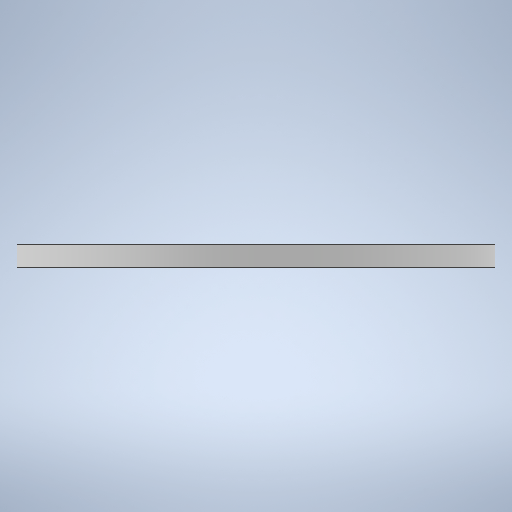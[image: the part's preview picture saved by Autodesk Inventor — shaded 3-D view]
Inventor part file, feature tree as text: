
AUTODESK INVENTOR PART (.ipt)
format: ipt  version: 2025.2 (Build 292293000, 293)  size: 529,408 bytes
history: native  units: in
note: dims shown in document units (in); Inventor stores cm internally (conversion verified against a paired STEP export)
features: sketch x7, extrude x5, hole x1, revolve x1
ambient origin geometry x8: Origin, YZ Plane, XZ Plane, XY Plane, X Axis, Y Axis, Z Axis, Center Point
bodies: Solid1 (feature_tree)
feature tree (14):
  sketch  "Sketch1"  dims[d0=11.811in d1=7.874in]
  extrude  "Extrusion1"  Depth=7.874in
  extrude  "Extrusion3"  Depth=0.0787in
  extrude  "Extrusion4"  Depth=3.937in TaperAngle=360.0deg
  sketch  "Sketch3"  dims[d14=0.2343in d15=3.937in d17=360.0deg]
  extrude  "Extrusion5"  Depth=11.0236in
  hole  "Hole1"  [1 undecoded]
  revolve  "Revolution1"  [1 undecoded]
  extrude  "Extrusion6"  Depth=0.0837in TaperAngle=0.0deg
  sketch  "Sketch Circular Pattern2"  dims[d8=0.0787in d9=0.0in d13=9.8425in]
  sketch  "Sketch Circular Pattern3"  dims[d19=9.498in d20=11.0236in]
  sketch  "Sketch4"  dims[d21=0.2343in d23=3.937in d25=360.0deg]
  sketch  "Sketch5"  dims[d27=0.1673in d28=0.0in d33=0.4232in d34=0.0in]
  sketch  "Sketch Circular Pattern5"  dims[d35=9.498in d36=0.0837in d37=0.0in d38=0.2343in d39=0.2362in d40=0.4124in d41=0.2904in d42=90.0deg d43=0.315in d44=0.8108in d45=0.1575in d46=0.1575in d48=0.5709in d49=0.1575in d50=0.1575in d51=360.0deg d52=0.3445in d53=0.2224in d54=0.0in d55=7.874in d56=3.937in d58=360.0deg d60=0.2343in]
note: 2 required parameter values undecoded (feature->parameter linkage not recoverable at this tier; creation-order binding heuristic only, values carry confidence <= 0.55)